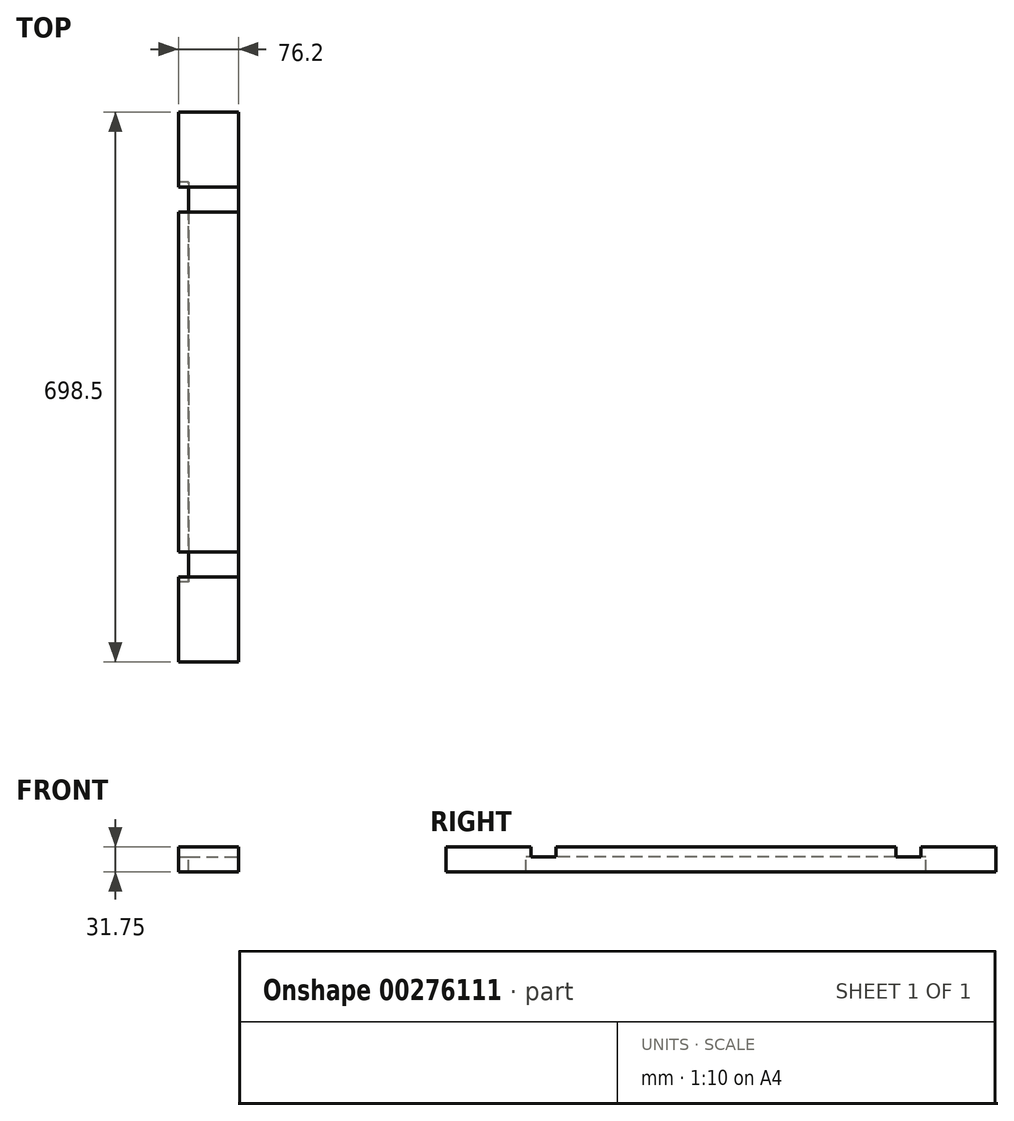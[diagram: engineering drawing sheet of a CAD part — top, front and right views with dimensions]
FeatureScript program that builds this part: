
annotation { "Feature Type Name" : "Feature", "Feature Type Description" : "" }
export const myFeature = defineFeature(function(context is Context, id is Id, definition is map)
    precondition{}
    {
        {
            var Q0;
            Q0=qCreatedBy(makeId("Front.planeOp"),FACE);
            var sketch = newSketch(context, id + "F0", { "sketchPlane" : qUnion([Q0])});
            skLineSegment(sketch, "E0.bottom", {"start": v(76.17, 0.22) * mm, "end": v(-0.03, 0.22) * mm});
            skLineSegment(sketch, "E0.top", {"start": v(76.17, 31.97) * mm, "end": v(-0.03, 31.97) * mm});
            skLineSegment(sketch, "E0.left", {"start": v(76.17, 0.22) * mm, "end": v(76.17, 31.97) * mm});
            skLineSegment(sketch, "E0.right", {"start": v(-0.03, 0.22) * mm, "end": v(-0.03, 31.97) * mm});
            skSolve(sketch);
        }
        {
            var Q0;
            Q0=makeQuery(id+"F0.imprint","IMPRINT",FACE,{"disambiguationData":[TD([[makeQuery(id+"F0.imprint","IMPRINT",EDGE,{"derivedFrom":sQuery(id+"F0.wireOp",EDGE,"E0.bottom")}),-1.0]])]});
            extrude(context, id + "F1", {"entities" : qUnion([Q0]), "depth" : 698.5 * mm});
        }
        {
            var Q0;
            Q0=makeQuery(id+"F1.opExtrude","SWEPT_FACE",FACE,{"disambiguationData":[OSD([sQuery(id+"F0.wireOp",EDGE,"E0.right")])]});
            var sketch = newSketch(context, id + "F2", { "sketchPlane" : qUnion([Q0])});
            skLineSegment(sketch, "E1.bottom", {"start": v(88.9, 0.22) * mm, "end": v(596.9, 0.22) * mm});
            skLineSegment(sketch, "E1.top", {"start": v(88.9, 19.27) * mm, "end": v(596.9, 19.27) * mm});
            skLineSegment(sketch, "E1.left", {"start": v(88.9, 0.22) * mm, "end": v(88.9, 19.27) * mm});
            skLineSegment(sketch, "E1.right", {"start": v(596.9, 0.22) * mm, "end": v(596.9, 19.27) * mm});
            skSolve(sketch);
        }
        {
            var Q0;
            Q0=makeQuery(id+"F2.imprint","IMPRINT",FACE,{"disambiguationData":[TD([[makeQuery(id+"F2.imprint","IMPRINT",EDGE,{"derivedFrom":sQuery(id+"F2.wireOp",EDGE,"E1.bottom")}),-1.0]])]});
            extrude(context, id + "F3", {"entities" : qUnion([Q0]), "operationType" : NewBodyOperationType.REMOVE, "oppositeDirection" : true, "depth" : 12.7 * mm});
        }
        {
            var Q0;
            Q0=makeQuery(id+"F1.opExtrude","SWEPT_FACE",FACE,{"disambiguationData":[OSD([sQuery(id+"F0.wireOp",EDGE,"E0.top")])]});
            var sketch = newSketch(context, id + "F4", { "sketchPlane" : qUnion([Q0])});
            skLineSegment(sketch, "E2", {"start": v(-0.03, -590.55) * mm, "end": v(76.17, -590.55) * mm});
            skLineSegment(sketch, "E3", {"start": v(-0.03, -558.8) * mm, "end": v(76.17, -558.8) * mm});
            skLineSegment(sketch, "E4", {"start": v(-0.03, -127) * mm, "end": v(76.17, -127) * mm});
            skLineSegment(sketch, "E5", {"start": v(-0.03, -95.25) * mm, "end": v(76.17, -95.25) * mm});
            skSolve(sketch);
        }
        {
            var Q0;
            {var subQ0=sQuery(id+"F4.wireOp",EDGE,"E2");Q0=makeQuery(id+"F4.imprint","IMPRINT",FACE,{"disambiguationData":[TD([[makeQuery(id+"F4.imprint","IMPRINT",EDGE,{"derivedFrom":subQ0}),1.0]])]});}
            var Q1;
            {var subQ0=sQuery(id+"F4.wireOp",EDGE,"E4");Q1=makeQuery(id+"F4.imprint","IMPRINT",FACE,{"disambiguationData":[TD([[makeQuery(id+"F4.imprint","IMPRINT",EDGE,{"derivedFrom":subQ0}),1.0]])]});}
            extrude(context, id + "F5", {"entities" : qUnion([Q0, Q1]), "operationType" : NewBodyOperationType.REMOVE, "oppositeDirection" : true, "depth" : 12.7 * mm});
        }
    });
